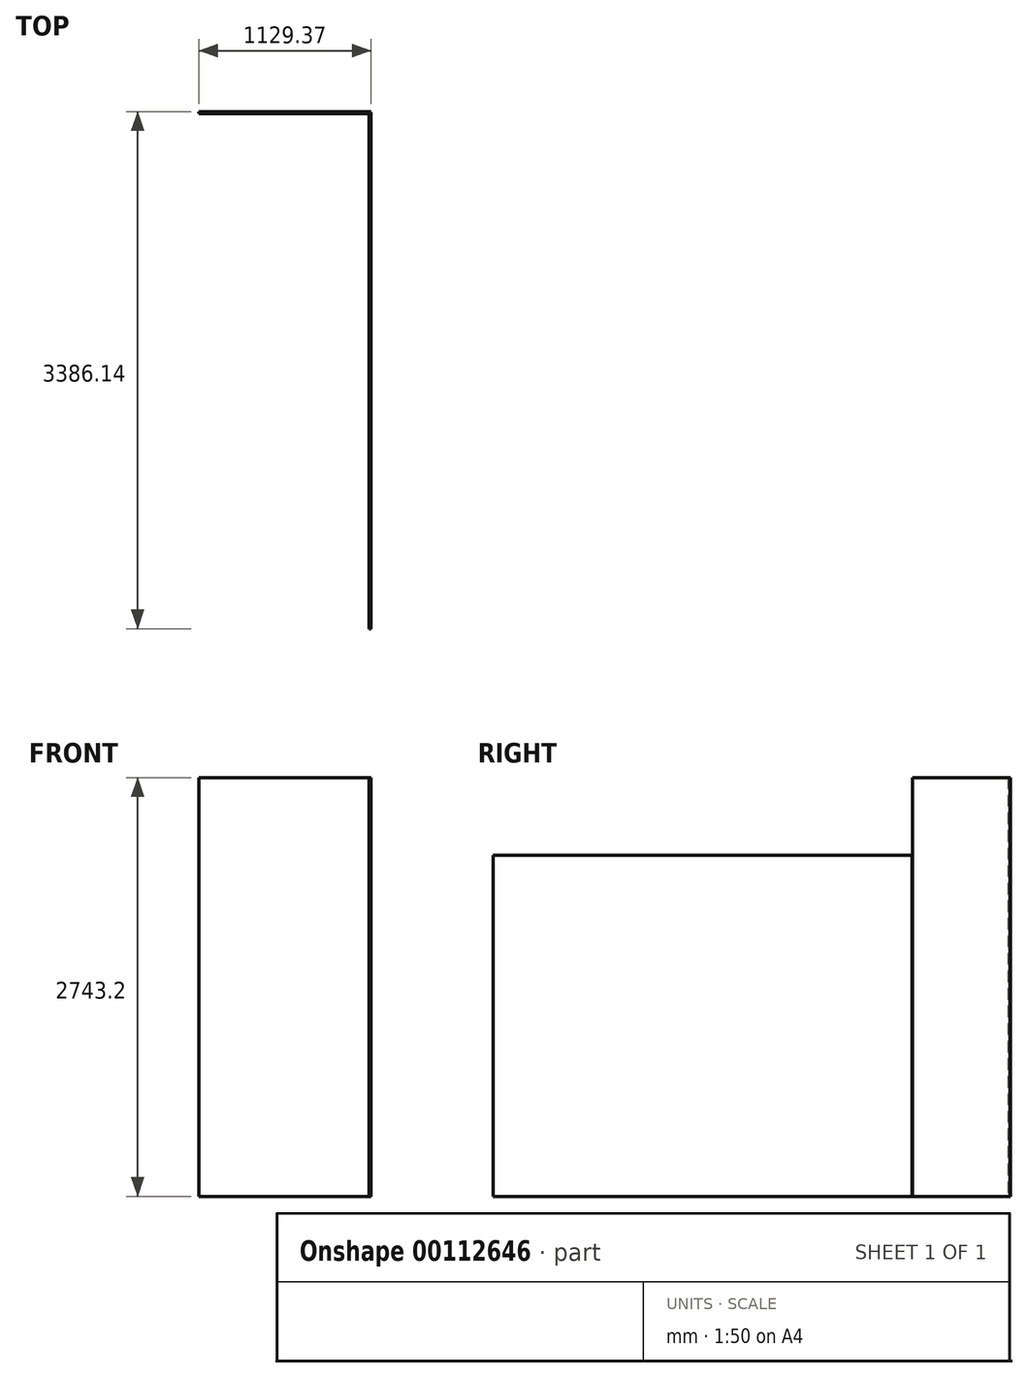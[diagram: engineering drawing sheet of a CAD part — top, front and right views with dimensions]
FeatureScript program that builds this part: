
annotation { "Feature Type Name" : "Feature", "Feature Type Description" : "" }
export const myFeature = defineFeature(function(context is Context, id is Id, definition is map)
    precondition{}
    {
        {
            var Q0;
            Q0=qCreatedBy(makeId("Top.planeOp"),FACE);
            var sketch = newSketch(context, id + "F0", { "sketchPlane" : qUnion([Q0])});
            skLineSegment(sketch, "E0", {"start": v(-10131.68, -2060.57) * mm, "end": v(10131.68, -2060.57) * mm});
            skLineSegment(sketch, "E1", {"start": v(-5919.73, 1965.33) * mm, "end": v(-6243.58, 1965.33) * mm});
            skLineSegment(sketch, "E2", {"start": v(-6072.13, 1965.33) * mm, "end": v(-6072.13, -2060.57) * mm});
            skLineSegment(sketch, "E3", {"start": v(-6243.58, 1965.33) * mm, "end": v(-6243.58, -2060.57) * mm});
            skLineSegment(sketch, "E4", {"start": v(-4910.08, 1963.74) * mm, "end": v(-4910.08, 1954.21) * mm});
            skLineSegment(sketch, "E5", {"start": v(-2460.57, 1965.33) * mm, "end": v(-3681.36, 1965.33) * mm});
            skLineSegment(sketch, "E6", {"start": v(-2460.57, 1952.63) * mm, "end": v(-3681.36, 1952.63) * mm});
            skLineSegment(sketch, "E7", {"start": v(-4922.78, 2060.57) * mm, "end": v(-2439.93, 2060.57) * mm});
            skLineSegment(sketch, "E8", {"start": v(-4922.78, 1857.38) * mm, "end": v(-2439.93, 1857.38) * mm});
            skLineSegment(sketch, "E9", {"start": v(-2446.28, 1857.38) * mm, "end": v(-2446.28, 2060.57) * mm});
            skLineSegment(sketch, "E10", {"start": v(-2439.93, 1857.38) * mm, "end": v(-2439.93, 2060.57) * mm});
            skLineSegment(sketch, "E11", {"start": v(-2439.68, 1863.72) * mm, "end": v(-2433.58, 1863.72) * mm});
            skLineSegment(sketch, "E12", {"start": v(-2262.13, -2060.57) * mm, "end": v(-2262.13, 1863.8) * mm});
            skLineSegment(sketch, "E13", {"start": v(-2379.39, 1895.64) * mm, "end": v(-2385.82, 1895.64) * mm});
            skLineSegment(sketch, "E14", {"start": v(-2433.58, 1984.38) * mm, "end": v(-2370.08, 1984.38) * mm});
            skArc(sketch, "E15", {"start": v(-2370.08, 1984.38) * mm, "mid": v(-2365.6, 1982.52) * mm, "end": v(-2363.73, 1978.03) * mm});
            skLineSegment(sketch, "E16", {"start": v(-2363.73, 1978.03) * mm, "end": v(-2363.73, 1939.93) * mm});
            skArc(sketch, "E17", {"start": v(-2363.73, 1939.93) * mm, "mid": v(-2365.6, 1935.43) * mm, "end": v(-2370.08, 1933.58) * mm});
            skLineSegment(sketch, "E18", {"start": v(-2370.08, 1933.58) * mm, "end": v(-2433.58, 1933.58) * mm});
            skArc(sketch, "E19", {"start": v(-2433.58, 1933.58) * mm, "mid": v(-2438.07, 1935.43) * mm, "end": v(-2439.93, 1939.93) * mm});
            skLineSegment(sketch, "E20", {"start": v(-2439.93, 1939.93) * mm, "end": v(-2439.93, 1978.03) * mm});
            skArc(sketch, "E21", {"start": v(-2439.93, 1978.03) * mm, "mid": v(-2438.07, 1982.52) * mm, "end": v(-2433.58, 1984.38) * mm});
            skLineSegment(sketch, "E22", {"start": v(-2433.58, 1978.03) * mm, "end": v(-2370.08, 1978.03) * mm});
            skLineSegment(sketch, "E23", {"start": v(-2370.08, 1978.03) * mm, "end": v(-2370.08, 1939.93) * mm});
            skLineSegment(sketch, "E24", {"start": v(-2370.08, 1939.93) * mm, "end": v(-2433.58, 1939.93) * mm});
            skLineSegment(sketch, "E25", {"start": v(-2433.58, 1939.93) * mm, "end": v(-2433.58, 1978.03) * mm});
            skLineSegment(sketch, "E26", {"start": v(-2404.8, 1895.64) * mm, "end": v(-2411.23, 1895.64) * mm});
            skLineSegment(sketch, "E27", {"start": v(-2411.23, 1895.64) * mm, "end": v(-2411.23, 1933.58) * mm});
            skLineSegment(sketch, "E28", {"start": v(-2411.23, 1933.58) * mm, "end": v(-2379.39, 1933.58) * mm});
            skLineSegment(sketch, "E29", {"start": v(-2379.39, 1933.58) * mm, "end": v(-2379.39, 1895.64) * mm});
            skLineSegment(sketch, "E30", {"start": v(-2385.82, 1895.64) * mm, "end": v(-2385.82, 1927.48) * mm});
            skLineSegment(sketch, "E31", {"start": v(-2385.82, 1927.48) * mm, "end": v(-2404.8, 1927.48) * mm});
            skLineSegment(sketch, "E32", {"start": v(-2404.8, 1927.48) * mm, "end": v(-2404.8, 1895.64) * mm});
            skLineSegment(sketch, "E33", {"start": v(-2433.58, -2060.57) * mm, "end": v(-2433.58, 1863.72) * mm});
            skLineSegment(sketch, "E34", {"start": v(-2262.13, 1863.8) * mm, "end": v(-2262.13, 2047.71) * mm});
            skLineSegment(sketch, "E35", {"start": v(-4922.78, 2060.57) * mm, "end": v(-4922.78, 1857.38) * mm});
            skLineSegment(sketch, "E36", {"start": v(-4929.13, 2060.57) * mm, "end": v(-4929.13, 1857.38) * mm});
            skLineSegment(sketch, "E37", {"start": v(-4935.48, 1933.58) * mm, "end": v(-4998.98, 1933.58) * mm});
            skArc(sketch, "E38", {"start": v(-4998.98, 1933.58) * mm, "mid": v(-5003.47, 1935.43) * mm, "end": v(-5005.33, 1939.93) * mm});
            skLineSegment(sketch, "E39", {"start": v(-5005.33, 1939.93) * mm, "end": v(-5005.33, 1978.03) * mm});
            skArc(sketch, "E40", {"start": v(-5005.33, 1978.03) * mm, "mid": v(-5003.47, 1982.52) * mm, "end": v(-4998.98, 1984.38) * mm});
            skLineSegment(sketch, "E41", {"start": v(-4998.98, 1984.38) * mm, "end": v(-4935.48, 1984.38) * mm});
            skArc(sketch, "E42", {"start": v(-4935.48, 1984.38) * mm, "mid": v(-4931, 1982.52) * mm, "end": v(-4929.13, 1978.03) * mm});
            skLineSegment(sketch, "E43", {"start": v(-4929.13, 1978.03) * mm, "end": v(-4929.13, 1939.93) * mm});
            skArc(sketch, "E44", {"start": v(-4929.13, 1939.93) * mm, "mid": v(-4931, 1935.43) * mm, "end": v(-4935.48, 1933.58) * mm});
            skLineSegment(sketch, "E45", {"start": v(-4935.48, 1939.93) * mm, "end": v(-4998.98, 1939.93) * mm});
            skLineSegment(sketch, "E46", {"start": v(-4998.98, 1939.93) * mm, "end": v(-4998.98, 1978.03) * mm});
            skLineSegment(sketch, "E47", {"start": v(-4998.98, 1978.03) * mm, "end": v(-4935.48, 1978.03) * mm});
            skLineSegment(sketch, "E48", {"start": v(-4935.48, 1978.03) * mm, "end": v(-4935.48, 1939.93) * mm});
            skLineSegment(sketch, "E49", {"start": v(-4929.13, 2060.57) * mm, "end": v(-4922.78, 2060.57) * mm});
            skLineSegment(sketch, "E50", {"start": v(-4929.13, 1857.38) * mm, "end": v(-4922.78, 1857.38) * mm});
            skLineSegment(sketch, "E51", {"start": v(-2363.47, 1864.99) * mm, "end": v(-2363.47, 2047.71) * mm});
            skLineSegment(sketch, "E52", {"start": v(-2363.47, 2047.71) * mm, "end": v(-2262.13, 2047.71) * mm});
            skLineSegment(sketch, "E53", {"start": v(-2262.13, 1863.8) * mm, "end": v(-2282.35, 1863.8) * mm});
            skLineSegment(sketch, "E54", {"start": v(-2282.35, 2029.08) * mm, "end": v(-2282.35, 1863.8) * mm});
            skLineSegment(sketch, "E55", {"start": v(-2282.35, 2029.08) * mm, "end": v(-2344.84, 2029.08) * mm});
            skLineSegment(sketch, "E56", {"start": v(-2344.84, 1864.99) * mm, "end": v(-2344.84, 2029.08) * mm});
            skLineSegment(sketch, "E57", {"start": v(-2433.58, 1863.72) * mm, "end": v(-2414.54, 1863.72) * mm});
            skLineSegment(sketch, "E58", {"start": v(-2414.54, 1863.72) * mm, "end": v(-2414.54, -2060.57) * mm});
            skLineSegment(sketch, "E59", {"start": v(-2262.13, 1863.72) * mm, "end": v(-2390.57, 1863.72) * mm});
            skLineSegment(sketch, "E60", {"start": v(-2284.23, 1863.72) * mm, "end": v(-2284.23, -2060.57) * mm});
            skLineSegment(sketch, "E61", {"start": v(-2344.84, 1864.99) * mm, "end": v(-2363.47, 1864.99) * mm});
            skLineSegment(sketch, "E62", {"start": v(-2400.05, 1863.72) * mm, "end": v(-2414.54, 1863.72) * mm});
            skLineSegment(sketch, "E63", {"start": v(-2388.96, 1916.4) * mm, "end": v(-2388.96, -61.76) * mm});
            skLineSegment(sketch, "E64", {"start": v(-2401.66, 1916.4) * mm, "end": v(-2401.66, -61.76) * mm});
            skLineSegment(sketch, "E65", {"start": v(-3686.12, 1963.74) * mm, "end": v(-3686.12, 1954.21) * mm});
            skLineSegment(sketch, "E66", {"start": v(-3687.7, 1965.33) * mm, "end": v(-4908.5, 1965.33) * mm});
            skLineSegment(sketch, "E67", {"start": v(-3687.7, 1952.63) * mm, "end": v(-4908.5, 1952.63) * mm});
            skLineSegment(sketch, "E68", {"start": v(-4908.5, 1965.33) * mm, "end": v(-4910.08, 1963.74) * mm});
            skLineSegment(sketch, "E69", {"start": v(-4908.5, 1952.63) * mm, "end": v(-4910.08, 1954.21) * mm});
            skLineSegment(sketch, "E70", {"start": v(-3687.7, 1965.33) * mm, "end": v(-3686.12, 1963.74) * mm});
            skLineSegment(sketch, "E71", {"start": v(-3687.7, 1952.63) * mm, "end": v(-3686.12, 1954.21) * mm});
            skLineSegment(sketch, "E72", {"start": v(-3682.94, 1963.74) * mm, "end": v(-3682.94, 1954.21) * mm});
            skLineSegment(sketch, "E73", {"start": v(-3681.36, 1965.33) * mm, "end": v(-3682.94, 1963.74) * mm});
            skLineSegment(sketch, "E74", {"start": v(-3681.36, 1952.63) * mm, "end": v(-3682.94, 1954.21) * mm});
            skLineSegment(sketch, "E75", {"start": v(-2458.98, 1963.74) * mm, "end": v(-2458.98, 1954.21) * mm});
            skLineSegment(sketch, "E76", {"start": v(-2460.57, 1965.33) * mm, "end": v(-2458.98, 1963.74) * mm});
            skLineSegment(sketch, "E77", {"start": v(-2460.57, 1952.63) * mm, "end": v(-2458.98, 1954.21) * mm});
            skLineSegment(sketch, "E78", {"start": v(-2400.07, 1918) * mm, "end": v(-2390.54, 1918) * mm});
            skLineSegment(sketch, "E79", {"start": v(-2401.66, 1916.4) * mm, "end": v(-2400.07, 1918) * mm});
            skLineSegment(sketch, "E80", {"start": v(-2388.96, 1916.4) * mm, "end": v(-2390.54, 1918) * mm});
            skLineSegment(sketch, "E81", {"start": v(-4910.08, 1958.98) * mm, "end": v(-3686.12, 1958.98) * mm});
            skLineSegment(sketch, "E82", {"start": v(-3682.94, 1958.98) * mm, "end": v(-2458.98, 1958.98) * mm});
            skLineSegment(sketch, "E83", {"start": v(-2395.3, 1918) * mm, "end": v(-2395.3, -63.35) * mm});
            skLineSegment(sketch, "E84", {"start": v(-2400.07, -2047.88) * mm, "end": v(-2390.54, -2047.88) * mm});
            skLineSegment(sketch, "E85", {"start": v(-2401.66, -2046.29) * mm, "end": v(-2400.07, -2047.88) * mm});
            skLineSegment(sketch, "E86", {"start": v(-2388.96, -2046.29) * mm, "end": v(-2390.54, -2047.88) * mm});
            skLineSegment(sketch, "E87", {"start": v(1224.02, -2060.57) * mm, "end": v(1224.02, 1863.72) * mm});
            skLineSegment(sketch, "E88", {"start": v(-1252.48, 1963.74) * mm, "end": v(-1252.48, 1954.21) * mm});
            skLineSegment(sketch, "E89", {"start": v(1197.03, 1965.33) * mm, "end": v(-23.76, 1965.33) * mm});
            skLineSegment(sketch, "E90", {"start": v(-30.1, 1965.33) * mm, "end": v(-1250.9, 1965.33) * mm});
            skLineSegment(sketch, "E91", {"start": v(1197.03, 1952.63) * mm, "end": v(-23.76, 1952.63) * mm});
            skLineSegment(sketch, "E92", {"start": v(-30.1, 1952.63) * mm, "end": v(-1250.9, 1952.63) * mm});
            skLineSegment(sketch, "E93", {"start": v(-1265.18, 2060.57) * mm, "end": v(1217.67, 2060.57) * mm});
            skLineSegment(sketch, "E94", {"start": v(-1265.18, 1857.38) * mm, "end": v(1217.67, 1857.38) * mm});
            skLineSegment(sketch, "E95", {"start": v(1211.32, 1857.38) * mm, "end": v(1211.32, 2060.57) * mm});
            skLineSegment(sketch, "E96", {"start": v(1217.67, 1857.38) * mm, "end": v(1217.67, 2060.57) * mm});
            skLineSegment(sketch, "E97", {"start": v(1217.92, 1863.72) * mm, "end": v(1224.02, 1863.72) * mm});
            skLineSegment(sketch, "E98", {"start": v(1395.47, -2060.57) * mm, "end": v(1395.47, 1863.8) * mm});
            skLineSegment(sketch, "E99", {"start": v(1278.21, 1895.64) * mm, "end": v(1271.78, 1895.64) * mm});
            skLineSegment(sketch, "E100", {"start": v(1224.02, 1984.38) * mm, "end": v(1287.52, 1984.38) * mm});
            skArc(sketch, "E101", {"start": v(1287.52, 1984.38) * mm, "mid": v(1292, 1982.52) * mm, "end": v(1293.87, 1978.03) * mm});
            skLineSegment(sketch, "E102", {"start": v(1293.87, 1978.03) * mm, "end": v(1293.87, 1939.93) * mm});
            skArc(sketch, "E103", {"start": v(1293.87, 1939.93) * mm, "mid": v(1292, 1935.43) * mm, "end": v(1287.52, 1933.58) * mm});
            skLineSegment(sketch, "E104", {"start": v(1287.52, 1933.58) * mm, "end": v(1224.02, 1933.58) * mm});
            skArc(sketch, "E105", {"start": v(1224.02, 1933.58) * mm, "mid": v(1219.53, 1935.43) * mm, "end": v(1217.67, 1939.93) * mm});
            skLineSegment(sketch, "E106", {"start": v(1217.67, 1939.93) * mm, "end": v(1217.67, 1978.03) * mm});
            skArc(sketch, "E107", {"start": v(1217.67, 1978.03) * mm, "mid": v(1219.53, 1982.52) * mm, "end": v(1224.02, 1984.38) * mm});
            skLineSegment(sketch, "E108", {"start": v(1224.02, 1978.03) * mm, "end": v(1287.52, 1978.03) * mm});
            skLineSegment(sketch, "E109", {"start": v(1287.52, 1978.03) * mm, "end": v(1287.52, 1939.93) * mm});
            skLineSegment(sketch, "E110", {"start": v(1287.52, 1939.93) * mm, "end": v(1224.02, 1939.93) * mm});
            skLineSegment(sketch, "E111", {"start": v(1224.02, 1939.93) * mm, "end": v(1224.02, 1978.03) * mm});
            skLineSegment(sketch, "E112", {"start": v(1252.8, 1895.64) * mm, "end": v(1246.37, 1895.64) * mm});
            skLineSegment(sketch, "E113", {"start": v(1246.37, 1895.64) * mm, "end": v(1246.37, 1933.58) * mm});
            skLineSegment(sketch, "E114", {"start": v(1246.37, 1933.58) * mm, "end": v(1278.21, 1933.58) * mm});
            skLineSegment(sketch, "E115", {"start": v(1278.21, 1933.58) * mm, "end": v(1278.21, 1895.64) * mm});
            skLineSegment(sketch, "E116", {"start": v(1271.78, 1895.64) * mm, "end": v(1271.78, 1927.48) * mm});
            skLineSegment(sketch, "E117", {"start": v(1271.78, 1927.48) * mm, "end": v(1252.8, 1927.48) * mm});
            skLineSegment(sketch, "E118", {"start": v(1252.8, 1927.48) * mm, "end": v(1252.8, 1895.64) * mm});
            skLineSegment(sketch, "E119", {"start": v(1395.47, 1863.8) * mm, "end": v(1395.47, 2047.71) * mm});
            skLineSegment(sketch, "E120", {"start": v(-1265.18, 2060.57) * mm, "end": v(-1265.18, 1857.38) * mm});
            skLineSegment(sketch, "E121", {"start": v(-1271.53, 2060.57) * mm, "end": v(-1271.53, 1857.38) * mm});
            skLineSegment(sketch, "E122", {"start": v(-1277.88, 1933.58) * mm, "end": v(-1341.38, 1933.58) * mm});
            skArc(sketch, "E123", {"start": v(-1341.38, 1933.58) * mm, "mid": v(-1345.87, 1935.43) * mm, "end": v(-1347.73, 1939.93) * mm});
            skLineSegment(sketch, "E124", {"start": v(-1347.73, 1939.93) * mm, "end": v(-1347.73, 1978.03) * mm});
            skArc(sketch, "E125", {"start": v(-1347.73, 1978.03) * mm, "mid": v(-1345.87, 1982.52) * mm, "end": v(-1341.38, 1984.38) * mm});
            skLineSegment(sketch, "E126", {"start": v(-1341.38, 1984.38) * mm, "end": v(-1277.88, 1984.38) * mm});
            skArc(sketch, "E127", {"start": v(-1277.88, 1984.38) * mm, "mid": v(-1273.4, 1982.52) * mm, "end": v(-1271.53, 1978.03) * mm});
            skLineSegment(sketch, "E128", {"start": v(-1271.53, 1978.03) * mm, "end": v(-1271.53, 1939.93) * mm});
            skArc(sketch, "E129", {"start": v(-1271.53, 1939.93) * mm, "mid": v(-1273.4, 1935.43) * mm, "end": v(-1277.88, 1933.58) * mm});
            skLineSegment(sketch, "E130", {"start": v(-1277.88, 1939.93) * mm, "end": v(-1341.38, 1939.93) * mm});
            skLineSegment(sketch, "E131", {"start": v(-1341.38, 1939.93) * mm, "end": v(-1341.38, 1978.03) * mm});
            skLineSegment(sketch, "E132", {"start": v(-1341.38, 1978.03) * mm, "end": v(-1277.88, 1978.03) * mm});
            skLineSegment(sketch, "E133", {"start": v(-1277.88, 1978.03) * mm, "end": v(-1277.88, 1939.93) * mm});
            skLineSegment(sketch, "E134", {"start": v(-1271.53, 2060.57) * mm, "end": v(-1265.18, 2060.57) * mm});
            skLineSegment(sketch, "E135", {"start": v(-1271.53, 1857.38) * mm, "end": v(-1265.18, 1857.38) * mm});
            skLineSegment(sketch, "E136", {"start": v(1294.13, 1864.99) * mm, "end": v(1294.13, 2047.71) * mm});
            skLineSegment(sketch, "E137", {"start": v(1294.13, 2047.71) * mm, "end": v(1395.47, 2047.71) * mm});
            skLineSegment(sketch, "E138", {"start": v(1395.47, 1863.8) * mm, "end": v(1375.25, 1863.8) * mm});
            skLineSegment(sketch, "E139", {"start": v(1375.25, 2029.08) * mm, "end": v(1375.25, 1863.8) * mm});
            skLineSegment(sketch, "E140", {"start": v(1375.25, 2029.08) * mm, "end": v(1312.76, 2029.08) * mm});
            skLineSegment(sketch, "E141", {"start": v(1312.76, 1864.99) * mm, "end": v(1312.76, 2029.08) * mm});
            skLineSegment(sketch, "E142", {"start": v(1224.02, 1863.72) * mm, "end": v(1243.06, 1863.72) * mm});
            skLineSegment(sketch, "E143", {"start": v(1243.06, 1863.72) * mm, "end": v(1243.06, -2060.57) * mm});
            skLineSegment(sketch, "E144", {"start": v(1395.47, 1863.72) * mm, "end": v(1267.03, 1863.72) * mm});
            skLineSegment(sketch, "E145", {"start": v(1257.55, 1863.72) * mm, "end": v(1243.06, 1863.72) * mm});
            skLineSegment(sketch, "E146", {"start": v(1373.37, 1863.72) * mm, "end": v(1373.37, -2060.57) * mm});
            skLineSegment(sketch, "E147", {"start": v(1312.76, 1864.99) * mm, "end": v(1294.13, 1864.99) * mm});
            skLineSegment(sketch, "E148", {"start": v(1268.64, 1916.4) * mm, "end": v(1268.64, -61.76) * mm});
            skLineSegment(sketch, "E149", {"start": v(1255.94, 1916.4) * mm, "end": v(1255.94, -61.76) * mm});
            skLineSegment(sketch, "E150", {"start": v(-28.52, 1963.74) * mm, "end": v(-28.52, 1954.21) * mm});
            skLineSegment(sketch, "E151", {"start": v(-1250.9, 1965.33) * mm, "end": v(-1252.48, 1963.74) * mm});
            skLineSegment(sketch, "E152", {"start": v(-1250.9, 1952.63) * mm, "end": v(-1252.48, 1954.21) * mm});
            skLineSegment(sketch, "E153", {"start": v(-30.1, 1965.33) * mm, "end": v(-28.52, 1963.74) * mm});
            skLineSegment(sketch, "E154", {"start": v(-30.1, 1952.63) * mm, "end": v(-28.52, 1954.21) * mm});
            skLineSegment(sketch, "E155", {"start": v(-25.34, 1963.74) * mm, "end": v(-25.34, 1954.21) * mm});
            skLineSegment(sketch, "E156", {"start": v(-23.76, 1965.33) * mm, "end": v(-25.34, 1963.74) * mm});
            skLineSegment(sketch, "E157", {"start": v(-23.76, 1952.63) * mm, "end": v(-25.34, 1954.21) * mm});
            skLineSegment(sketch, "E158", {"start": v(1198.62, 1963.74) * mm, "end": v(1198.62, 1954.21) * mm});
            skLineSegment(sketch, "E159", {"start": v(1197.03, 1965.33) * mm, "end": v(1198.62, 1963.74) * mm});
            skLineSegment(sketch, "E160", {"start": v(1197.03, 1952.63) * mm, "end": v(1198.62, 1954.21) * mm});
            skLineSegment(sketch, "E161", {"start": v(1257.53, 1918) * mm, "end": v(1267.06, 1918) * mm});
            skLineSegment(sketch, "E162", {"start": v(1255.94, 1916.4) * mm, "end": v(1257.53, 1918) * mm});
            skLineSegment(sketch, "E163", {"start": v(1268.64, 1916.4) * mm, "end": v(1267.06, 1918) * mm});
            skLineSegment(sketch, "E164", {"start": v(-1252.48, 1958.98) * mm, "end": v(-28.52, 1958.98) * mm});
            skLineSegment(sketch, "E165", {"start": v(-25.34, 1958.98) * mm, "end": v(1198.62, 1958.98) * mm});
            skLineSegment(sketch, "E166", {"start": v(1262.3, 1918) * mm, "end": v(1262.3, -63.35) * mm});
            skLineSegment(sketch, "E167", {"start": v(1257.53, -2047.88) * mm, "end": v(1267.06, -2047.88) * mm});
            skLineSegment(sketch, "E168", {"start": v(1255.94, -2046.29) * mm, "end": v(1257.53, -2047.88) * mm});
            skLineSegment(sketch, "E169", {"start": v(1268.64, -2046.29) * mm, "end": v(1267.06, -2047.88) * mm});
            skLineSegment(sketch, "E170", {"start": v(2405.12, 1963.74) * mm, "end": v(2405.12, 1954.21) * mm});
            skLineSegment(sketch, "E171", {"start": v(5793.77, 1965.33) * mm, "end": v(4666.65, 1965.33) * mm});
            skLineSegment(sketch, "E172", {"start": v(2392.42, 2060.57) * mm, "end": v(5891.27, 2060.57) * mm});
            skLineSegment(sketch, "E173", {"start": v(2392.42, 1857.38) * mm, "end": v(5688.07, 1857.38) * mm});
            skLineSegment(sketch, "E174", {"start": v(2392.42, 2060.57) * mm, "end": v(2392.42, 1857.38) * mm});
            skLineSegment(sketch, "E175", {"start": v(2386.07, 2060.57) * mm, "end": v(2386.07, 1857.38) * mm});
            skLineSegment(sketch, "E176", {"start": v(2379.72, 1933.58) * mm, "end": v(2316.22, 1933.58) * mm});
            skArc(sketch, "E177", {"start": v(2316.22, 1933.58) * mm, "mid": v(2311.73, 1935.43) * mm, "end": v(2309.87, 1939.93) * mm});
            skLineSegment(sketch, "E178", {"start": v(2309.87, 1939.93) * mm, "end": v(2309.87, 1978.03) * mm});
            skArc(sketch, "E179", {"start": v(2309.87, 1978.03) * mm, "mid": v(2311.73, 1982.52) * mm, "end": v(2316.22, 1984.38) * mm});
            skLineSegment(sketch, "E180", {"start": v(2316.22, 1984.38) * mm, "end": v(2379.72, 1984.38) * mm});
            skArc(sketch, "E181", {"start": v(2379.72, 1984.38) * mm, "mid": v(2384.2, 1982.52) * mm, "end": v(2386.07, 1978.03) * mm});
            skLineSegment(sketch, "E182", {"start": v(2386.07, 1978.03) * mm, "end": v(2386.07, 1939.93) * mm});
            skArc(sketch, "E183", {"start": v(2386.07, 1939.93) * mm, "mid": v(2384.2, 1935.43) * mm, "end": v(2379.72, 1933.58) * mm});
            skLineSegment(sketch, "E184", {"start": v(2379.72, 1939.93) * mm, "end": v(2316.22, 1939.93) * mm});
            skLineSegment(sketch, "E185", {"start": v(2316.22, 1939.93) * mm, "end": v(2316.22, 1978.03) * mm});
            skLineSegment(sketch, "E186", {"start": v(2316.22, 1978.03) * mm, "end": v(2379.72, 1978.03) * mm});
            skLineSegment(sketch, "E187", {"start": v(2379.72, 1978.03) * mm, "end": v(2379.72, 1939.93) * mm});
            skLineSegment(sketch, "E188", {"start": v(2386.07, 2060.57) * mm, "end": v(2392.42, 2060.57) * mm});
            skLineSegment(sketch, "E189", {"start": v(2386.07, 1857.38) * mm, "end": v(2392.42, 1857.38) * mm});
            skLineSegment(sketch, "E190", {"start": v(2406.7, 1965.33) * mm, "end": v(2405.12, 1963.74) * mm});
            skLineSegment(sketch, "E191", {"start": v(2406.7, 1952.63) * mm, "end": v(2405.12, 1954.21) * mm});
            skLineSegment(sketch, "E192", {"start": v(2405.12, 1958.98) * mm, "end": v(3533.17, 1958.98) * mm});
            skLineSegment(sketch, "E193", {"start": v(5783.32, -2046.29) * mm, "end": v(5783.32, -1423.99) * mm});
            skLineSegment(sketch, "E194", {"start": v(5796.02, -2046.29) * mm, "end": v(5796.02, -1423.99) * mm});
            skLineSegment(sketch, "E195", {"start": v(5891.27, 2060.57) * mm, "end": v(5891.27, -2060.57) * mm});
            skLineSegment(sketch, "E196", {"start": v(5688.07, 1857.38) * mm, "end": v(5688.07, -2060.57) * mm});
            skLineSegment(sketch, "E197", {"start": v(5784.9, -2047.88) * mm, "end": v(5794.43, -2047.88) * mm});
            skLineSegment(sketch, "E198", {"start": v(5783.32, -2046.29) * mm, "end": v(5784.9, -2047.88) * mm});
            skLineSegment(sketch, "E199", {"start": v(5796.02, -2046.29) * mm, "end": v(5794.43, -2047.88) * mm});
            skLineSegment(sketch, "E200", {"start": v(-2400.07, -63.35) * mm, "end": v(-2390.54, -63.35) * mm});
            skLineSegment(sketch, "E201", {"start": v(-2400.07, -66.53) * mm, "end": v(-2390.54, -66.53) * mm});
            skLineSegment(sketch, "E202", {"start": v(-2388.96, -68.11) * mm, "end": v(-2388.96, -2046.29) * mm});
            skLineSegment(sketch, "E203", {"start": v(-2395.3, -66.53) * mm, "end": v(-2395.3, -2047.88) * mm});
            skLineSegment(sketch, "E204", {"start": v(-2401.66, -68.11) * mm, "end": v(-2401.66, -2046.29) * mm});
            skLineSegment(sketch, "E205", {"start": v(-2401.66, -68.11) * mm, "end": v(-2400.07, -66.53) * mm});
            skLineSegment(sketch, "E206", {"start": v(-2401.66, -61.76) * mm, "end": v(-2400.07, -63.35) * mm});
            skLineSegment(sketch, "E207", {"start": v(-2390.54, -66.53) * mm, "end": v(-2388.96, -68.11) * mm});
            skLineSegment(sketch, "E208", {"start": v(-2390.54, -63.35) * mm, "end": v(-2388.96, -61.76) * mm});
            skLineSegment(sketch, "E209", {"start": v(5796.02, 1322.39) * mm, "end": v(5783.32, 1322.39) * mm});
            skLineSegment(sketch, "E210", {"start": v(5796.02, -1420.81) * mm, "end": v(5783.32, -1420.81) * mm});
            skLineSegment(sketch, "E211", {"start": v(5796.02, -1423.99) * mm, "end": v(5783.32, -1423.99) * mm});
            skLineSegment(sketch, "E212", {"start": v(5796.02, -1420.81) * mm, "end": v(5796.02, 1322.39) * mm});
            skLineSegment(sketch, "E213", {"start": v(5789.67, -1423.99) * mm, "end": v(5789.67, -2047.88) * mm});
            skLineSegment(sketch, "E214", {"start": v(5783.32, -1420.81) * mm, "end": v(5783.32, 1322.39) * mm});
            skLineSegment(sketch, "E215", {"start": v(5796.02, 1325.56) * mm, "end": v(5783.32, 1325.56) * mm});
            skLineSegment(sketch, "E216", {"start": v(5796.02, 1325.56) * mm, "end": v(5796.02, 1963.08) * mm});
            skLineSegment(sketch, "E217", {"start": v(5789.67, 1322.39) * mm, "end": v(5789.67, -1420.81) * mm});
            skLineSegment(sketch, "E218", {"start": v(5783.32, 1325.56) * mm, "end": v(5783.32, 1950.38) * mm});
            skLineSegment(sketch, "E219", {"start": v(5783.32, 1950.38) * mm, "end": v(5796.02, 1963.08) * mm});
            skLineSegment(sketch, "E220", {"start": v(5781.07, 1952.63) * mm, "end": v(5793.77, 1965.33) * mm});
            skLineSegment(sketch, "E221", {"start": v(5789.67, 1963.08) * mm, "end": v(5789.67, 1325.56) * mm});
            skLineSegment(sketch, "E222", {"start": v(5781.07, 1952.63) * mm, "end": v(4666.65, 1952.63) * mm});
            skLineSegment(sketch, "E223", {"start": v(4666.65, 1952.63) * mm, "end": v(4666.65, 1965.33) * mm});
            skLineSegment(sketch, "E224", {"start": v(4663.47, 1952.63) * mm, "end": v(4663.47, 1965.33) * mm});
            skLineSegment(sketch, "E225", {"start": v(3536.35, 1952.63) * mm, "end": v(3536.35, 1965.33) * mm});
            skLineSegment(sketch, "E226", {"start": v(3533.17, 1952.63) * mm, "end": v(3533.17, 1965.33) * mm});
            skLineSegment(sketch, "E227", {"start": v(3533.17, 1952.63) * mm, "end": v(2406.7, 1952.63) * mm});
            skLineSegment(sketch, "E228", {"start": v(3533.17, 1965.33) * mm, "end": v(2406.7, 1965.33) * mm});
            skLineSegment(sketch, "E229", {"start": v(3536.35, 1958.98) * mm, "end": v(4663.47, 1958.98) * mm});
            skLineSegment(sketch, "E230", {"start": v(4663.47, 1965.33) * mm, "end": v(3536.35, 1965.33) * mm});
            skLineSegment(sketch, "E231", {"start": v(4666.65, 1958.98) * mm, "end": v(5793.77, 1958.98) * mm});
            skLineSegment(sketch, "E232", {"start": v(4663.47, 1952.63) * mm, "end": v(3536.35, 1952.63) * mm});
            skLineSegment(sketch, "E233", {"start": v(1257.53, -66.53) * mm, "end": v(1267.06, -66.53) * mm});
            skLineSegment(sketch, "E234", {"start": v(1257.53, -63.35) * mm, "end": v(1267.06, -63.35) * mm});
            skLineSegment(sketch, "E235", {"start": v(1255.94, -68.11) * mm, "end": v(1257.53, -66.53) * mm});
            skLineSegment(sketch, "E236", {"start": v(1255.94, -61.76) * mm, "end": v(1257.53, -63.35) * mm});
            skLineSegment(sketch, "E237", {"start": v(1267.06, -66.53) * mm, "end": v(1268.64, -68.11) * mm});
            skLineSegment(sketch, "E238", {"start": v(1267.06, -63.35) * mm, "end": v(1268.64, -61.76) * mm});
            skLineSegment(sketch, "E239", {"start": v(1255.94, -68.11) * mm, "end": v(1255.94, -2046.29) * mm});
            skLineSegment(sketch, "E240", {"start": v(1262.3, -66.53) * mm, "end": v(1262.3, -2047.88) * mm});
            skLineSegment(sketch, "E241", {"start": v(1268.64, -68.11) * mm, "end": v(1268.64, -2046.29) * mm});
            skSolve(sketch);
        }
        {
            var Q0;
            {var subQ0=sQuery(id+"F0.wireOp",EDGE,"E222");Q0=makeQuery(id+"F0.imprint","IMPRINT",FACE,{"disambiguationData":[TD([[makeQuery(id+"F0.imprint","IMPRINT",EDGE,{"derivedFrom":subQ0}),-1.0]])]});}
            var Q1;
            {var subQ1=sQuery(id+"F0.wireOp",EDGE,"E171");Q1=makeQuery(id+"F0.imprint","IMPRINT",FACE,{"disambiguationData":[TD([[makeQuery(id+"F0.imprint","IMPRINT",EDGE,{"derivedFrom":subQ1}),1.0]])]});}
            extrude(context, id + "F1", {"entities" : qUnion([Q0, Q1]), "depth" : 2743.2 * mm});
        }
        {
            var Q0;
            {var subQ0=sQuery(id+"F0.wireOp",EDGE,"E218");Q0=makeQuery(id+"F0.imprint","IMPRINT",FACE,{"disambiguationData":[TD([[makeQuery(id+"F0.imprint","IMPRINT",EDGE,{"derivedFrom":subQ0}),-1.0]])]});}
            var Q1;
            {var subQ5=sQuery(id+"F0.wireOp",EDGE,"E216");Q1=makeQuery(id+"F0.imprint","IMPRINT",FACE,{"disambiguationData":[TD([[makeQuery(id+"F0.imprint","IMPRINT",EDGE,{"derivedFrom":subQ5}),1.0]])]});}
            extrude(context, id + "F2", {"entities" : qUnion([Q0, Q1]), "depth" : 2743.2 * mm});
        }
        {
            var Q0;
            {var subQ0=sQuery(id+"F0.wireOp",EDGE,"E214");Q0=makeQuery(id+"F0.imprint","IMPRINT",FACE,{"disambiguationData":[TD([[makeQuery(id+"F0.imprint","IMPRINT",EDGE,{"derivedFrom":subQ0}),-1.0]])]});}
            var Q1;
            {var subQ0=sQuery(id+"F0.wireOp",EDGE,"E212");Q1=makeQuery(id+"F0.imprint","IMPRINT",FACE,{"disambiguationData":[TD([[makeQuery(id+"F0.imprint","IMPRINT",EDGE,{"derivedFrom":subQ0}),1.0]])]});}
            extrude(context, id + "F3", {"entities" : qUnion([Q0, Q1]), "depth" : 2235.2 * mm});
        }
    });
